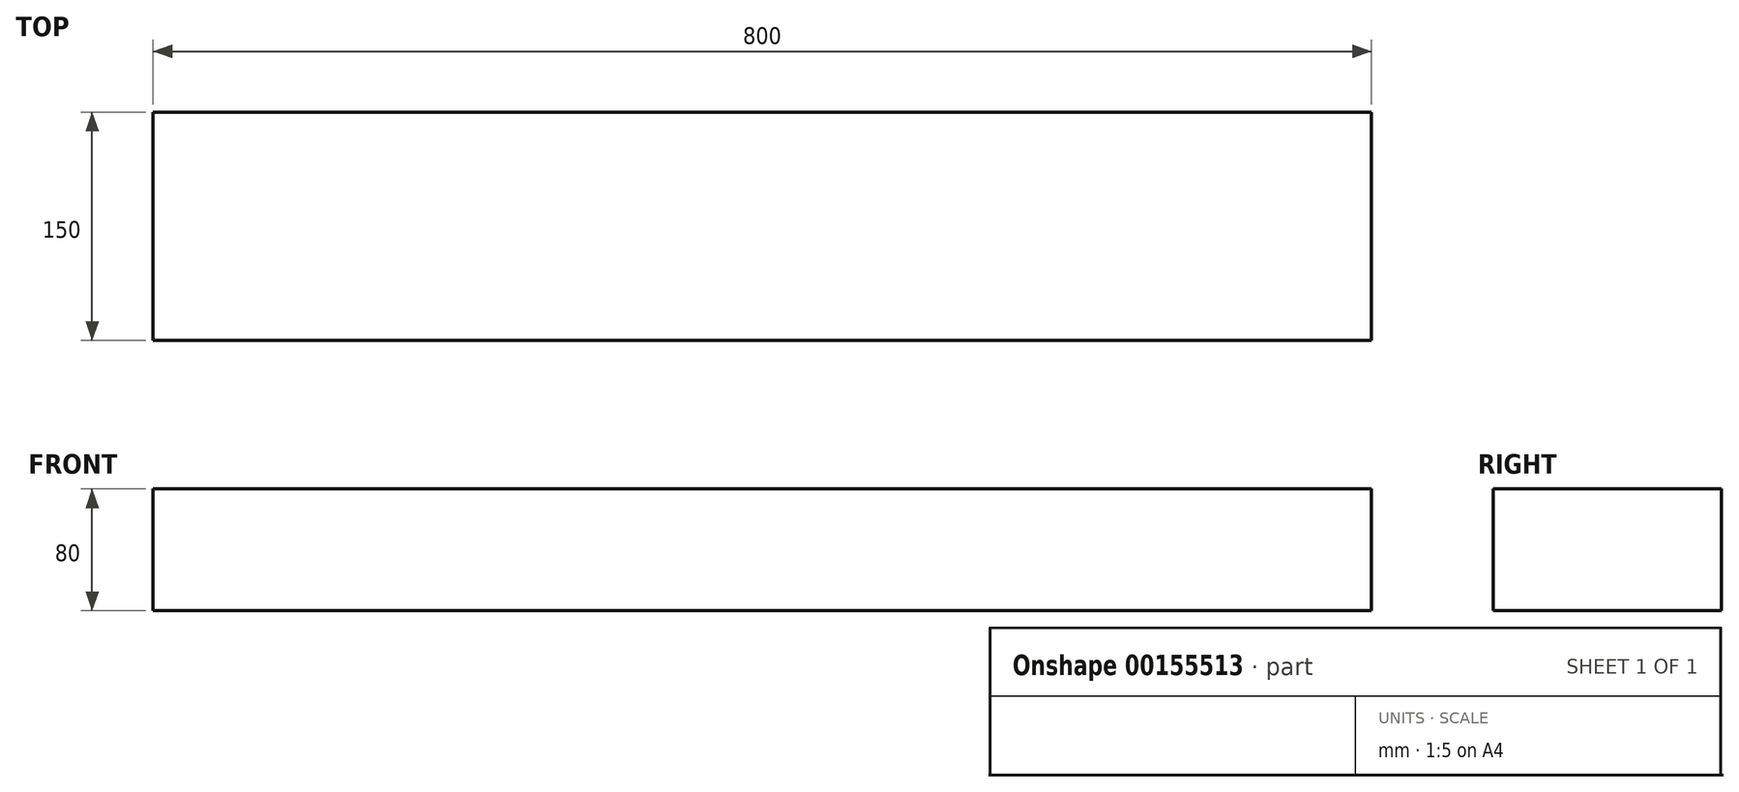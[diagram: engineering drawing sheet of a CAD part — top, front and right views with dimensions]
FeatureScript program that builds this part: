
annotation { "Feature Type Name" : "Feature", "Feature Type Description" : "" }
export const myFeature = defineFeature(function(context is Context, id is Id, definition is map)
    precondition{}
    {
        {
            var Q0;
            Q0=qCreatedBy(makeId("Top.planeOp"),FACE);
            var sketch = newSketch(context, id + "F0", { "sketchPlane" : qUnion([Q0])});
            skLineSegment(sketch, "E0.bottom", {"start": v(0, 0) * mm, "end": v(800, 0) * mm});
            skLineSegment(sketch, "E0.top", {"start": v(0, 150) * mm, "end": v(800, 150) * mm});
            skLineSegment(sketch, "E0.left", {"start": v(0, 0) * mm, "end": v(0, 150) * mm});
            skLineSegment(sketch, "E0.right", {"start": v(800, 0) * mm, "end": v(800, 150) * mm});
            skSolve(sketch);
        }
        {
            var Q0;
            Q0=makeQuery(id+"F0.imprint","IMPRINT",FACE,{"disambiguationData":[TD([[makeQuery(id+"F0.imprint","IMPRINT",EDGE,{"derivedFrom":sQuery(id+"F0.wireOp",EDGE,"E0.bottom")}),1.0]])]});
            extrude(context, id + "F1", {"entities" : qUnion([Q0]), "depth" : 80 * mm});
        }
    });
